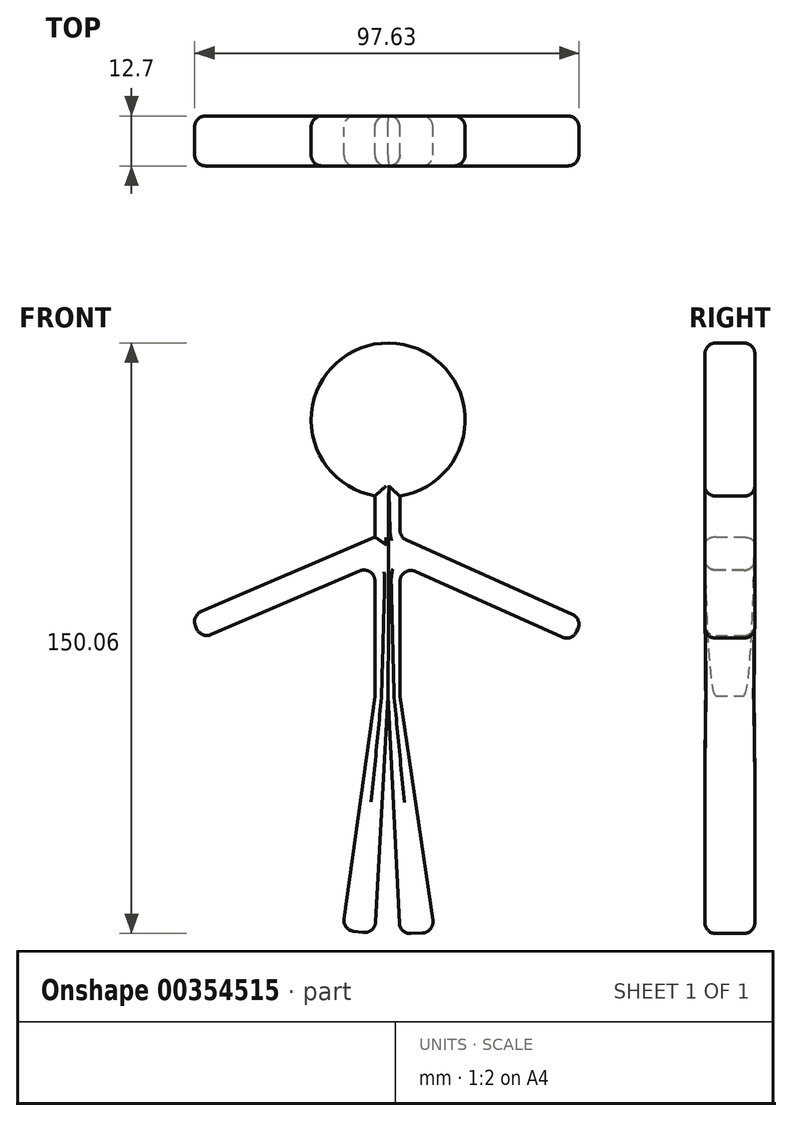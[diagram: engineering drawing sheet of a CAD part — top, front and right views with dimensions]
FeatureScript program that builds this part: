
annotation { "Feature Type Name" : "Feature", "Feature Type Description" : "" }
export const myFeature = defineFeature(function(context is Context, id is Id, definition is map)
    precondition{}
    {
        {
            var Q0;
            Q0=qCreatedBy(makeId("Front.planeOp"),FACE);
            var sketch = newSketch(context, id + "F0", { "sketchPlane" : qUnion([Q0])});
            skCircle(sketch, "E0", {"center": v(0, 58.6) * mm, "radius": 19.56 * mm});
            skLineSegment(sketch, "E1.bottom", {"start": v(-3.36, 39.34) * mm, "end": v(2.99, 39.34) * mm});
            skLineSegment(sketch, "E1.top", {"start": v(-3.36, -11.46) * mm, "end": v(2.99, -11.46) * mm});
            skLineSegment(sketch, "E1.left", {"start": v(-3.36, 39.34) * mm, "end": v(-3.36, -11.46) * mm});
            skLineSegment(sketch, "E1.right", {"start": v(2.99, 39.34) * mm, "end": v(2.99, -11.46) * mm});
            skLineSegment(sketch, "E2", {"start": v(-3.36, -11.46) * mm, "end": v(-11.62, -70.88) * mm});
            skLineSegment(sketch, "E3", {"start": v(-11.62, -70.88) * mm, "end": v(-3.36, -72.03) * mm});
            skLineSegment(sketch, "E4", {"start": v(-3.36, -72.03) * mm, "end": v(0, -11.46) * mm});
            skLineSegment(sketch, "E5", {"start": v(0, -11.46) * mm, "end": v(2.99, -72.03) * mm});
            skLineSegment(sketch, "E6", {"start": v(2.99, -72.03) * mm, "end": v(11.8, -71.6) * mm});
            skLineSegment(sketch, "E7", {"start": v(11.8, -71.6) * mm, "end": v(2.99, -11.46) * mm});
            skLineSegment(sketch, "E8", {"start": v(2.99, 28.84) * mm, "end": v(49.35, 8.08) * mm});
            skLineSegment(sketch, "E9", {"start": v(49.35, 8.08) * mm, "end": v(46.76, 2.29) * mm});
            skLineSegment(sketch, "E10", {"start": v(46.76, 2.29) * mm, "end": v(2.99, 21.89) * mm});
            skLineSegment(sketch, "E11", {"start": v(-3.36, 28.84) * mm, "end": v(-50.05, 8.83) * mm});
            skLineSegment(sketch, "E12", {"start": v(-50.05, 8.83) * mm, "end": v(-47.55, 2.99) * mm});
            skLineSegment(sketch, "E13", {"start": v(-47.55, 2.99) * mm, "end": v(-3.36, 21.94) * mm});
            skSolve(sketch);
        }
        {
            var Q0;
            Q0 = qSketchRegion(id + "F0", true);
            extrude(context, id + "F1", {"entities" : qUnion([Q0]), "depth" : 12.7 * mm});
        }
        {
            var Q0;
            Q0=makeQuery(id+"F1.opExtrude","CAP_EDGE",EDGE,{"disambiguationData":[OSD([sQuery(id+"F0.wireOp",EDGE,"E0")])],"isStart":false});
            var Q1;
            Q1=makeQuery(id+"F1.opExtrude","CAP_EDGE",EDGE,{"disambiguationData":[OSD([sQuery(id+"F0.wireOp",EDGE,"E0")])],"isStart":true});
            var Q2;
            {var subQ0=sQuery(id+"F0.wireOp",EDGE,"E1.left");Q2=makeQuery(id+"F1.opExtrude","CAP_EDGE",EDGE,{"disambiguationData":[OSD([subQ0]),TDD([makeQuery(id+"F0.imprint","IMPRINT",EDGE,{"disambiguationData":[TD([[makeQuery(id+"F0.imprint","INTERSECT",VERTEX,{"derivedFrom":[subQ0,sQuery(id+"F0.wireOp",EDGE,"E11")]}),1.0]])],"derivedFrom":subQ0})])],"isStart":false});}
            var Q3;
            {var subQ0=sQuery(id+"F0.wireOp",EDGE,"E1.right");Q3=makeQuery(id+"F1.opExtrude","CAP_EDGE",EDGE,{"disambiguationData":[OSD([subQ0]),TDD([makeQuery(id+"F0.imprint","IMPRINT",EDGE,{"disambiguationData":[TD([[makeQuery(id+"F0.imprint","INTERSECT",VERTEX,{"derivedFrom":[subQ0,sQuery(id+"F0.wireOp",EDGE,"E8")]}),1.0]])],"derivedFrom":subQ0})])],"isStart":true});}
            var Q4;
            Q4=makeQuery(id+"F1.opExtrude","SWEPT_EDGE",EDGE,{"disambiguationData":[OSD([sQuery(id+"F0.wireOp",EDGE,"E1.right"),sQuery(id+"F0.wireOp",EDGE,"E8")])]});
            var Q5;
            {var subQ0=sQuery(id+"F0.wireOp",EDGE,"E1.left");Q5=makeQuery(id+"F1.opExtrude","CAP_EDGE",EDGE,{"disambiguationData":[OSD([subQ0]),TDD([makeQuery(id+"F0.imprint","IMPRINT",EDGE,{"disambiguationData":[TD([[makeQuery(id+"F0.imprint","INTERSECT",VERTEX,{"derivedFrom":[subQ0,sQuery(id+"F0.wireOp",EDGE,"E11")]}),1.0]])],"derivedFrom":subQ0})])],"isStart":true});}
            var Q6;
            Q6=makeQuery(id+"F1.opExtrude","CAP_EDGE",EDGE,{"disambiguationData":[OSD([sQuery(id+"F0.wireOp",EDGE,"E11")])],"isStart":true});
            var Q7;
            Q7=makeQuery(id+"F1.opExtrude","CAP_EDGE",EDGE,{"disambiguationData":[OSD([sQuery(id+"F0.wireOp",EDGE,"E13")])],"isStart":true});
            var Q8;
            {var subQ0=sQuery(id+"F0.wireOp",EDGE,"E1.right");Q8=makeQuery(id+"F1.opExtrude","CAP_EDGE",EDGE,{"disambiguationData":[OSD([subQ0]),TDD([makeQuery(id+"F0.imprint","IMPRINT",EDGE,{"disambiguationData":[TD([[makeQuery(id+"F0.imprint","INTERSECT",VERTEX,{"derivedFrom":[subQ0,sQuery(id+"F0.wireOp",EDGE,"E8")]}),1.0]])],"derivedFrom":subQ0})])],"isStart":false});}
            var Q9;
            Q9=makeQuery(id+"F1.opExtrude","CAP_EDGE",EDGE,{"disambiguationData":[OSD([sQuery(id+"F0.wireOp",EDGE,"E13")])],"isStart":false});
            var Q10;
            Q10=makeQuery(id+"F1.opExtrude","CAP_EDGE",EDGE,{"disambiguationData":[OSD([sQuery(id+"F0.wireOp",EDGE,"E10")])],"isStart":false});
            var Q11;
            Q11=makeQuery(id+"F1.opExtrude","CAP_EDGE",EDGE,{"disambiguationData":[OSD([sQuery(id+"F0.wireOp",EDGE,"E10")])],"isStart":true});
            var Q12;
            {var subQ0=sQuery(id+"F0.wireOp",EDGE,"E1.left");Q12=makeQuery(id+"F1.opExtrude","CAP_EDGE",EDGE,{"disambiguationData":[OSD([subQ0]),TDD([makeQuery(id+"F0.imprint","IMPRINT",EDGE,{"disambiguationData":[TD([[makeQuery(id+"F0.imprint","INTERSECT",VERTEX,{"derivedFrom":[subQ0,sQuery(id+"F0.wireOp",EDGE,"E13")]}),-1.0]])],"derivedFrom":subQ0})])],"isStart":false});}
            var Q13;
            {var subQ0=sQuery(id+"F0.wireOp",EDGE,"E1.right");Q13=makeQuery(id+"F1.opExtrude","CAP_EDGE",EDGE,{"disambiguationData":[OSD([subQ0]),TDD([makeQuery(id+"F0.imprint","IMPRINT",EDGE,{"disambiguationData":[TD([[makeQuery(id+"F0.imprint","INTERSECT",VERTEX,{"derivedFrom":[subQ0,sQuery(id+"F0.wireOp",EDGE,"E10")]}),-1.0]])],"derivedFrom":subQ0})])],"isStart":false});}
            var Q14;
            {var subQ0=sQuery(id+"F0.wireOp",EDGE,"E1.right");Q14=makeQuery(id+"F1.opExtrude","CAP_EDGE",EDGE,{"disambiguationData":[OSD([subQ0]),TDD([makeQuery(id+"F0.imprint","IMPRINT",EDGE,{"disambiguationData":[TD([[makeQuery(id+"F0.imprint","INTERSECT",VERTEX,{"derivedFrom":[subQ0,sQuery(id+"F0.wireOp",EDGE,"E10")]}),-1.0]])],"derivedFrom":subQ0})])],"isStart":true});}
            var Q15;
            {var subQ0=sQuery(id+"F0.wireOp",EDGE,"E1.left");Q15=makeQuery(id+"F1.opExtrude","CAP_EDGE",EDGE,{"disambiguationData":[OSD([subQ0]),TDD([makeQuery(id+"F0.imprint","IMPRINT",EDGE,{"disambiguationData":[TD([[makeQuery(id+"F0.imprint","INTERSECT",VERTEX,{"derivedFrom":[subQ0,sQuery(id+"F0.wireOp",EDGE,"E13")]}),-1.0]])],"derivedFrom":subQ0})])],"isStart":true});}
            var Q16;
            Q16=makeQuery(id+"F1.opExtrude","SWEPT_EDGE",EDGE,{"disambiguationData":[OSD([sQuery(id+"F0.wireOp",EDGE,"E8"),sQuery(id+"F0.wireOp",EDGE,"E9")])]});
            var Q17;
            Q17=makeQuery(id+"F1.opExtrude","SWEPT_EDGE",EDGE,{"disambiguationData":[OSD([sQuery(id+"F0.wireOp",EDGE,"E9"),sQuery(id+"F0.wireOp",EDGE,"E10")])]});
            var Q18;
            Q18=makeQuery(id+"F1.opExtrude","CAP_EDGE",EDGE,{"disambiguationData":[OSD([sQuery(id+"F0.wireOp",EDGE,"E9")])],"isStart":true});
            var Q19;
            Q19=makeQuery(id+"F1.opExtrude","CAP_EDGE",EDGE,{"disambiguationData":[OSD([sQuery(id+"F0.wireOp",EDGE,"E9")])],"isStart":false});
            var Q20;
            Q20=makeQuery(id+"F1.opExtrude","CAP_EDGE",EDGE,{"disambiguationData":[OSD([sQuery(id+"F0.wireOp",EDGE,"E8")])],"isStart":false});
            var Q21;
            Q21=makeQuery(id+"F1.opExtrude","SWEPT_EDGE",EDGE,{"disambiguationData":[OSD([sQuery(id+"F0.wireOp",EDGE,"E11"),sQuery(id+"F0.wireOp",EDGE,"E12")])]});
            var Q22;
            Q22=makeQuery(id+"F1.opExtrude","CAP_EDGE",EDGE,{"disambiguationData":[OSD([sQuery(id+"F0.wireOp",EDGE,"E12")])],"isStart":true});
            var Q23;
            Q23=makeQuery(id+"F1.opExtrude","SWEPT_EDGE",EDGE,{"disambiguationData":[OSD([sQuery(id+"F0.wireOp",EDGE,"E12"),sQuery(id+"F0.wireOp",EDGE,"E13")])]});
            var Q24;
            Q24=makeQuery(id+"F1.opExtrude","CAP_EDGE",EDGE,{"disambiguationData":[OSD([sQuery(id+"F0.wireOp",EDGE,"E2")])],"isStart":false});
            var Q25;
            Q25=makeQuery(id+"F1.opExtrude","CAP_EDGE",EDGE,{"disambiguationData":[OSD([sQuery(id+"F0.wireOp",EDGE,"E12")])],"isStart":false});
            var Q26;
            Q26=makeQuery(id+"F1.opExtrude","CAP_EDGE",EDGE,{"disambiguationData":[OSD([sQuery(id+"F0.wireOp",EDGE,"E11")])],"isStart":false});
            var Q27;
            Q27=makeQuery(id+"F1.opExtrude","CAP_FACE",FACE,{"disambiguationData":[OSD([sQuery(id+"F0.wireOp",EDGE,"E0"),sQuery(id+"F0.wireOp",EDGE,"E1.left"),sQuery(id+"F0.wireOp",EDGE,"E1.right"),sQuery(id+"F0.wireOp",EDGE,"E2"),sQuery(id+"F0.wireOp",EDGE,"E3"),sQuery(id+"F0.wireOp",EDGE,"E4"),sQuery(id+"F0.wireOp",EDGE,"E5"),sQuery(id+"F0.wireOp",EDGE,"E6"),sQuery(id+"F0.wireOp",EDGE,"E7"),sQuery(id+"F0.wireOp",EDGE,"E8"),sQuery(id+"F0.wireOp",EDGE,"E9"),sQuery(id+"F0.wireOp",EDGE,"E10"),sQuery(id+"F0.wireOp",EDGE,"E11"),sQuery(id+"F0.wireOp",EDGE,"E12"),sQuery(id+"F0.wireOp",EDGE,"E13")])],"isStart":false});
            var Q28;
            Q28=makeQuery(id+"F1.opExtrude","CAP_FACE",FACE,{"disambiguationData":[OSD([sQuery(id+"F0.wireOp",EDGE,"E0"),sQuery(id+"F0.wireOp",EDGE,"E1.left"),sQuery(id+"F0.wireOp",EDGE,"E1.right"),sQuery(id+"F0.wireOp",EDGE,"E2"),sQuery(id+"F0.wireOp",EDGE,"E3"),sQuery(id+"F0.wireOp",EDGE,"E4"),sQuery(id+"F0.wireOp",EDGE,"E5"),sQuery(id+"F0.wireOp",EDGE,"E6"),sQuery(id+"F0.wireOp",EDGE,"E7"),sQuery(id+"F0.wireOp",EDGE,"E8"),sQuery(id+"F0.wireOp",EDGE,"E9"),sQuery(id+"F0.wireOp",EDGE,"E10"),sQuery(id+"F0.wireOp",EDGE,"E11"),sQuery(id+"F0.wireOp",EDGE,"E12"),sQuery(id+"F0.wireOp",EDGE,"E13")])],"isStart":true});
            var Q29;
            Q29=makeQuery(id+"F1.opExtrude","SWEPT_FACE",FACE,{"disambiguationData":[OSD([sQuery(id+"F0.wireOp",EDGE,"E3")])]});
            var Q30;
            Q30=makeQuery(id+"F1.opExtrude","SWEPT_FACE",FACE,{"disambiguationData":[OSD([sQuery(id+"F0.wireOp",EDGE,"E6")])]});
            var Q31;
            {var subQ0=sQuery(id+"F0.wireOp",EDGE,"E1.right");Q31=makeQuery(id+"F1.opExtrude","SWEPT_FACE",FACE,{"disambiguationData":[OSD([subQ0]),TDD([makeQuery(id+"F0.imprint","IMPRINT",EDGE,{"disambiguationData":[TD([[makeQuery(id+"F0.imprint","INTERSECT",VERTEX,{"derivedFrom":[subQ0,sQuery(id+"F0.wireOp",EDGE,"E10")]}),-1.0]])],"derivedFrom":subQ0})])]});}
            var Q32;
            Q32=makeQuery(id+"F1.opExtrude","SWEPT_FACE",FACE,{"disambiguationData":[OSD([sQuery(id+"F0.wireOp",EDGE,"E7")])]});
            var Q33;
            {var subQ0=sQuery(id+"F0.wireOp",EDGE,"E1.left");Q33=makeQuery(id+"F1.opExtrude","SWEPT_FACE",FACE,{"disambiguationData":[OSD([subQ0]),TDD([makeQuery(id+"F0.imprint","IMPRINT",EDGE,{"disambiguationData":[TD([[makeQuery(id+"F0.imprint","INTERSECT",VERTEX,{"derivedFrom":[subQ0,sQuery(id+"F0.wireOp",EDGE,"E13")]}),-1.0]])],"derivedFrom":subQ0})])]});}
            var Q34;
            Q34=makeQuery(id+"F1.opExtrude","SWEPT_FACE",FACE,{"disambiguationData":[OSD([sQuery(id+"F0.wireOp",EDGE,"E2")])]});
            fillet(context, id + "F2", {"entities" : qUnion([Q0, Q1, Q2, Q3, Q4, Q5, Q6, Q7, Q8, Q9, Q10, Q11, Q12, Q13, Q14, Q15, Q16, Q17, Q18, Q19, Q20, Q21, Q22, Q23, Q24, Q25, Q26, Q27, Q28, Q29, Q30, Q31, Q32, Q33, Q34]), "radius" : 2.8 * mm, "tangentPropagation" : true, "allowEdgeOverflow" : false});
        }
    });
